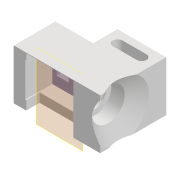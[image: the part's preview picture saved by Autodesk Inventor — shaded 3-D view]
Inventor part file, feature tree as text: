
AUTODESK INVENTOR PART (.ipt)
format: ipt  version: 2022 (Build 260153000, 153)  size: 198,656 bytes
history: native  units: mm
features: other x7, extrude x6, sketch x6, reference x5, plane x3, projected_geometry x3, chamfer x2
ambient origin geometry x8: Origin, YZ Plane, XZ Plane, XY Plane, X Axis, Y Axis, Z Axis, Center Point
bodies: Volumenkörper1 (feature_tree)
feature tree (32):
  plane  "Arbeitsebene1"
  plane  "Arbeitsebene2"
  extrude  "Extrusion1"  Depth=3.0mm
  sketch  "Skizze2"  dims[d2=4.0mm d3=12.0mm]
  plane  "Arbeitsebene3"
  extrude  "Extrusion2"  Depth=4.0mm
  extrude  "Extrusion3"  Depth=6.0mm
  extrude  "Extrusion4"  Depth=4.0mm
  extrude  "Extrusion5"  Depth=10.5mm TaperAngle=0.0deg
  extrude  "Extrusion6"  Depth=6.0mm TaperAngle=0.0deg
  chamfer  "Fase1"  Distance=20.0mm
  chamfer  "Fase2"  Distance=10.0mm
  sketch  "Skizze1"  dims[d0=5.0mm d1=3.0mm]
  reference  "Referenz1"
  reference  "Referenz2"
  projected_geometry  "Projizierte Kontur1"
  sketch  "Skizze3"  dims[d4=6.0mm d5=0.0mm d6=0.3mm]
  reference  "Referenz3"
  projected_geometry  "Projizierte Kontur2"
  sketch  "Skizze4"  dims[d7=4.0mm d8=0.0mm d9=1.0mm]
  reference  "Referenz5"
  sketch  "Skizze5"  dims[d10=5.5mm d11=0.0mm d13=10.5mm d14=0.0mm]
  reference  "Referenz6"
  sketch  "Skizze6"  dims[d15=4.0mm d16=0.0mm d17=6.0mm d18=0.0mm d19=20.0mm d20=10.0mm d21=4.0mm d22=5.5mm d23=0.0mm d24=5.0mm d25=2.0mm d26=45.0deg d27=4.0mm d28=2.0mm d29=45.0deg d30=13.5mm]
  projected_geometry  "Projizierte Kontur3"
  other  "<userpath>\Documents\GitHub\Guinardia\INVENTOR\Assemlby_Scanner_v0.iam"
  other  "Assemlby_Scanner_v0.iam"
  other  "Assembly_Huawei_P30_Scanninglens:1"
  other  "00_huawei_p30_Objectivelensassembly:1"
  other  "00_Huawei_P30_Lens_Adapterpcb:1"
  other  "00_SMAConnector_fiber copy:1"
  other  "Baugruppe1"
